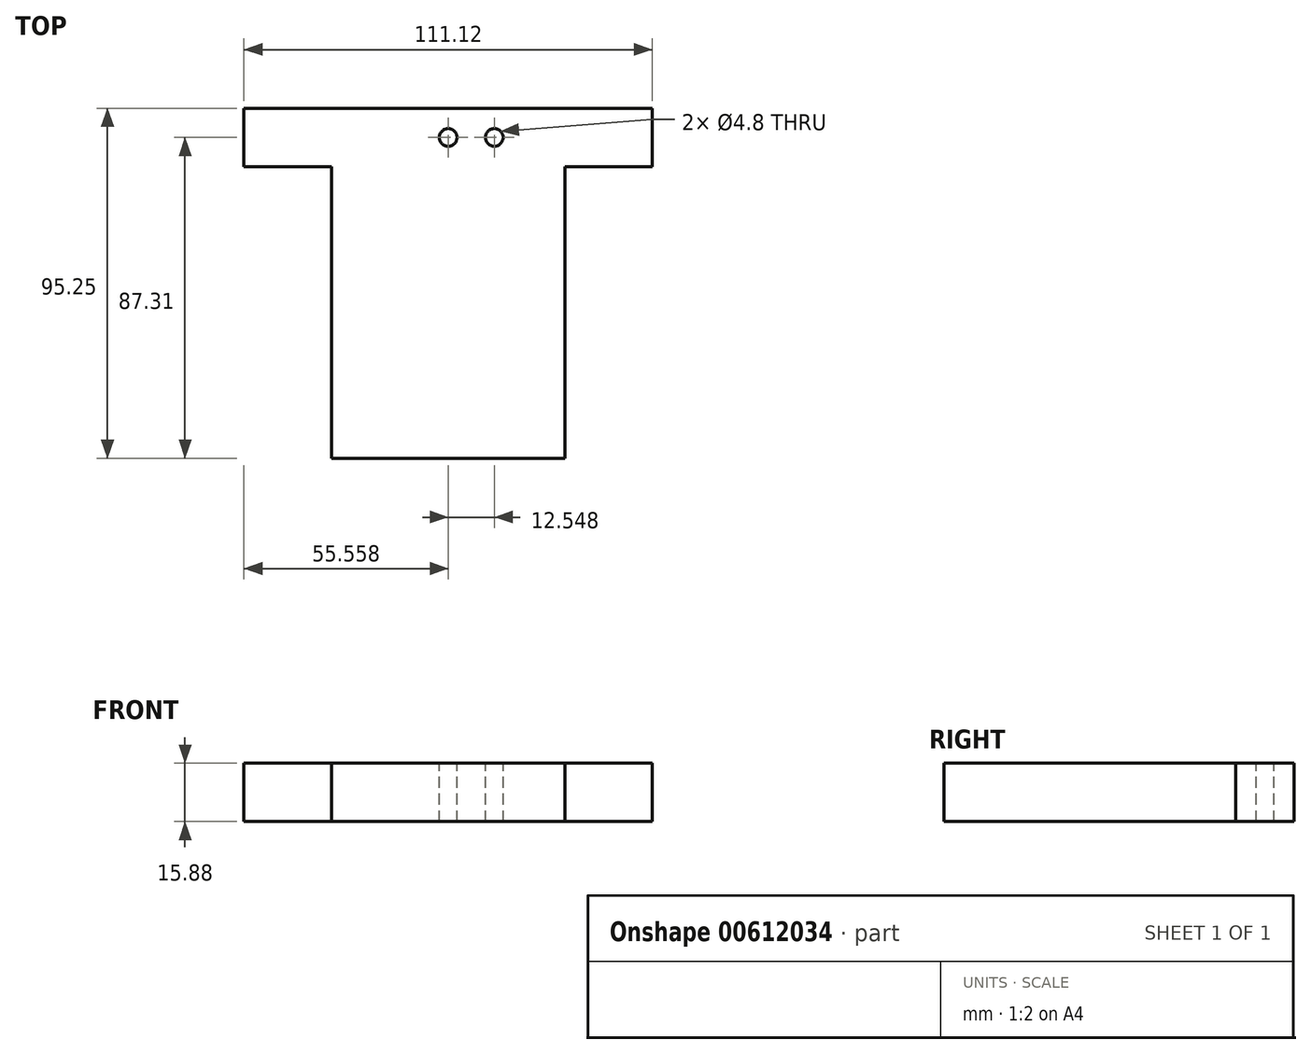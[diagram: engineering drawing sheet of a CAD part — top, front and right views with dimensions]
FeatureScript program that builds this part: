
annotation { "Feature Type Name" : "Feature", "Feature Type Description" : "" }
export const myFeature = defineFeature(function(context is Context, id is Id, definition is map)
    precondition{}
    {
        {
            var Q0;
            Q0=qCreatedBy(makeId("Top.planeOp"),FACE);
            var sketch = newSketch(context, id + "F0", { "sketchPlane" : qUnion([Q0])});
            skLineSegment(sketch, "E0", {"start": v(-33.82, 32.54) * mm, "end": v(29.68, 32.54) * mm});
            skLineSegment(sketch, "E1", {"start": v(29.68, 32.54) * mm, "end": v(29.68, -46.83) * mm});
            skLineSegment(sketch, "E2", {"start": v(29.68, -46.83) * mm, "end": v(-33.82, -46.83) * mm});
            skLineSegment(sketch, "E3", {"start": v(-33.82, -46.83) * mm, "end": v(-33.82, 32.54) * mm});
            skLineSegment(sketch, "E4", {"start": v(-33.82, 32.54) * mm, "end": v(-57.63, 32.54) * mm});
            skLineSegment(sketch, "E5", {"start": v(-57.63, 32.54) * mm, "end": v(-57.63, 48.42) * mm});
            skLineSegment(sketch, "E6", {"start": v(-57.63, 48.42) * mm, "end": v(53.5, 48.42) * mm});
            skLineSegment(sketch, "E7", {"start": v(53.5, 48.42) * mm, "end": v(53.5, 32.54) * mm});
            skLineSegment(sketch, "E8", {"start": v(53.5, 32.54) * mm, "end": v(29.68, 32.54) * mm});
            skSolve(sketch);
        }
        {
            var Q0;
            Q0 = qSketchRegion(id + "F0", true);
            extrude(context, id + "F1", {"entities" : qUnion([Q0]), "depth" : 15.88 * mm, "offsetDistance" : 25.4 * mm});
        }
        {
            var Q0;
            Q0=makeQuery(id+"F1.opExtrude","CAP_FACE",FACE,{"disambiguationData":[OSD([sQuery(id+"F0.wireOp",EDGE,"E1"),sQuery(id+"F0.wireOp",EDGE,"E2"),sQuery(id+"F0.wireOp",EDGE,"E3"),sQuery(id+"F0.wireOp",EDGE,"E4"),sQuery(id+"F0.wireOp",EDGE,"E5"),sQuery(id+"F0.wireOp",EDGE,"E6"),sQuery(id+"F0.wireOp",EDGE,"E7"),sQuery(id+"F0.wireOp",EDGE,"E8")])],"isStart":false});
            var sketch = newSketch(context, id + "F2", { "sketchPlane" : qUnion([Q0])});
            skCircle(sketch, "E9", {"center": v(-2.07, 40.48) * mm, "radius": 2.4 * mm});
            skPoint(sketch, "E9.centerSnap0", {"position": v(-57.63, 40.48) * mm});
            skPoint(sketch, "E9.centerSnap1", {"position": v(-2.07, 48.42) * mm});
            skCircle(sketch, "E10", {"center": v(10.48, 40.48) * mm, "radius": 2.4 * mm});
            skSolve(sketch);
        }
        {
            var Q0;
            Q0 = qSketchRegion(id + "F2", true);
            extrude(context, id + "F3", {"entities" : qUnion([Q0]), "operationType" : NewBodyOperationType.REMOVE, "endBound" : BoundingType.THROUGH_ALL, "oppositeDirection" : true, "depth" : 25.4 * mm, "offsetDistance" : 25.4 * mm});
        }
    });
